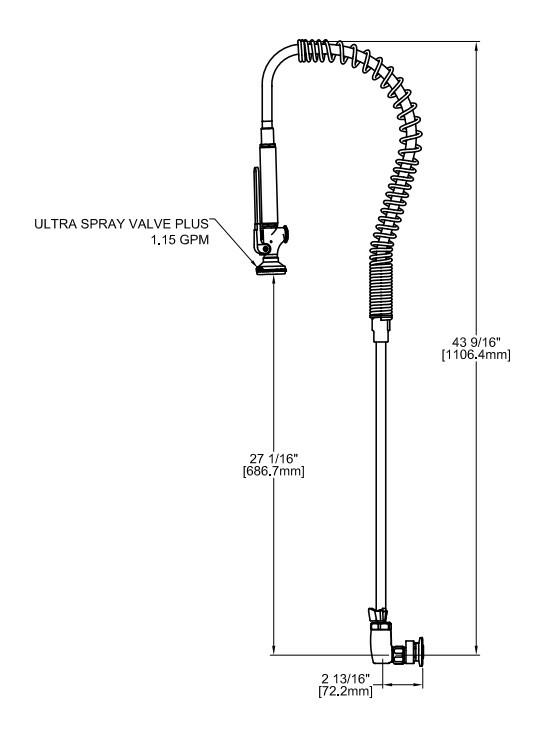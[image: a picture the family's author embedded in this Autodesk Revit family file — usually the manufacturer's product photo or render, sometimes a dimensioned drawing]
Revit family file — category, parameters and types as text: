
# Revit family: PICB-SP-SDDLL_21110
name_source: partatom
category: Plumbing Fixtures
units: mm (PartAtom-declared; Revit-internal decimal feet)

## family parameters
Always vertical = Yes
Cut with Voids When Loaded = No
OmniClass Number = 23.45.00.00
OmniClass Title = Sanitary, Laundry, and Cleaning Equipment
Part Type = Normal
Room Calculation Point = No
Round Connector Dimension = Use Diameter
Shared = No
Work Plane-Based = No

## types (1)
- PICB-SP-SDDLL_21110
    Cold Water Consumption = 0 GPM
    Cold Water Flow = 2 GPM
    Cold Water Maximum Pressure = 200.00 psi
    Cold Water Minimum Pressure = 80.00 psi
    Cold Water Size = 1/2"
    Cold Water Temperature Recommended = 40 °F
    Fixture Height = 4' - 0"
    Hot Water Consumption = 0 GPM
    Hot Water Flow = 2 GPM
    Hot Water Maximum Pressure = 200.00 psi
    Hot Water Minimum Pressure = 80.00 psi
    Hot Water Size = 1/2"
    Hot Water Temperature = 40 °F

## geometry (parser evidence)
native form markers: Sweep x20
no freeform markers — native parametric forms only
